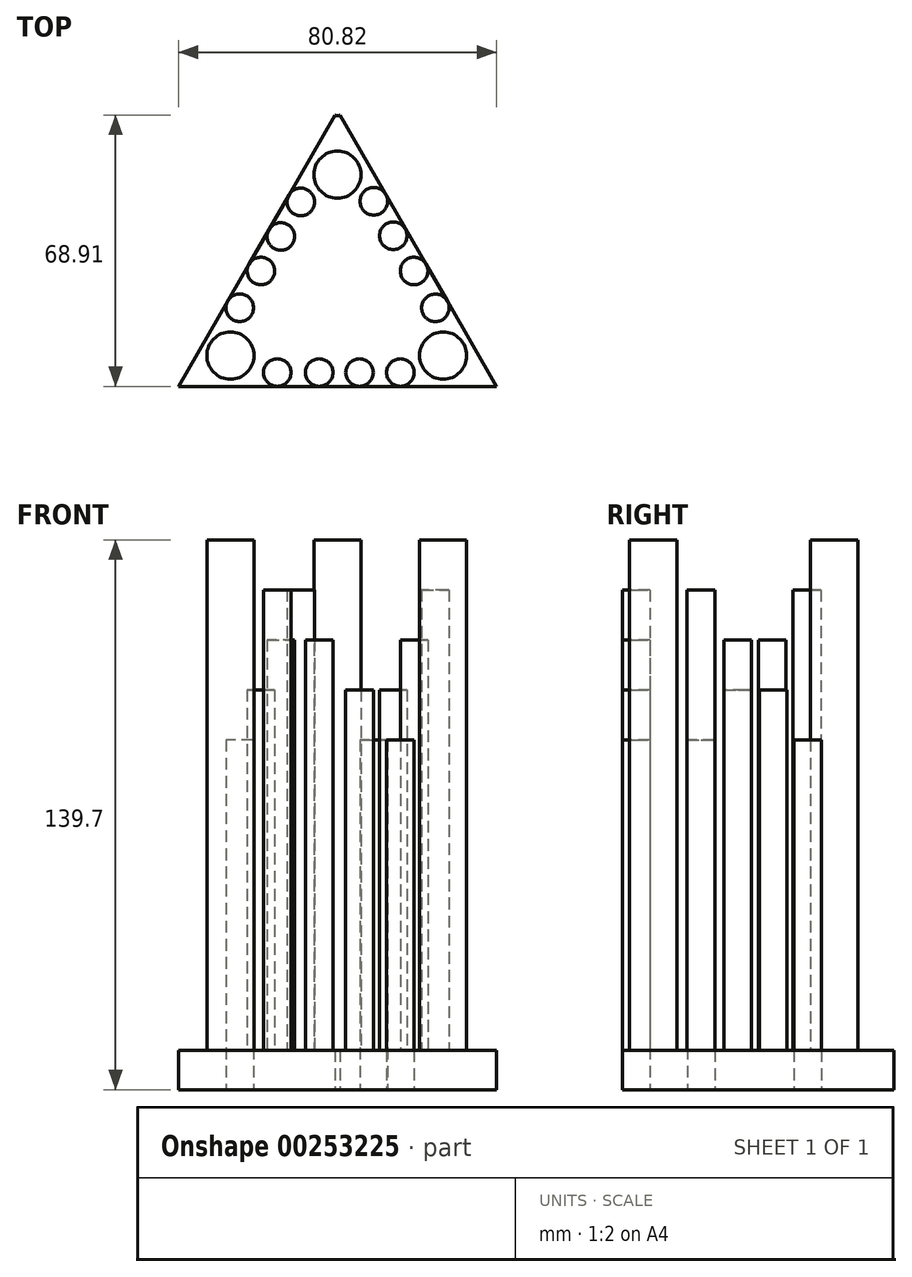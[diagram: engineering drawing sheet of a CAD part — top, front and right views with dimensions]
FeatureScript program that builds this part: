
annotation { "Feature Type Name" : "Feature", "Feature Type Description" : "" }
export const myFeature = defineFeature(function(context is Context, id is Id, definition is map)
    precondition{}
    {
        {
            var Q0;
            Q0=qCreatedBy(makeId("Top.planeOp"),FACE);
            var sketch = newSketch(context, id + "F0", { "sketchPlane" : qUnion([Q0])});
            skCircle(sketch, "E0.cCircle", {"center": v(0, 0) * mm, "radius": 23.33 * mm, "construction": true});
            skLineSegment(sketch, "E0.0", {"start": v(40.41, -23.33) * mm, "end": v(0, 46.67) * mm});
            skLineSegment(sketch, "E0.1", {"start": v(40.41, -23.33) * mm, "end": v(-40.41, -23.33) * mm});
            skLineSegment(sketch, "E0.2", {"start": v(0, 46.67) * mm, "end": v(-40.41, -23.33) * mm});
            skPoint(sketch, "E0.0.midPoint", {"position": v(20.2, 11.67) * mm});
            skCircle(sketch, "E1", {"center": v(0, 46.67) * mm, "radius": 1.25 * mm});
            skCircle(sketch, "E2", {"center": v(0, 30.46) * mm, "radius": 6 * mm});
            skCircle(sketch, "E3", {"center": v(-27.2, -15.52) * mm, "radius": 6 * mm});
            skCircle(sketch, "E4", {"center": v(26.82, -15.52) * mm, "radius": 6 * mm});
            skCircle(sketch, "E5", {"center": v(9.23, 23.69) * mm, "radius": 3.5 * mm});
            skCircle(sketch, "E6", {"center": v(14.17, 14.94) * mm, "radius": 3.5 * mm});
            skCircle(sketch, "E7", {"center": v(19.46, 5.97) * mm, "radius": 3.5 * mm});
            skCircle(sketch, "E8", {"center": v(15.98, -19.83) * mm, "radius": 3.5 * mm});
            skCircle(sketch, "E9", {"center": v(24.87, -3.4) * mm, "radius": 3.5 * mm});
            skCircle(sketch, "E10", {"center": v(-9.32, 23.52) * mm, "radius": 3.5 * mm});
            skCircle(sketch, "E11", {"center": v(-14.4, 14.74) * mm, "radius": 3.5 * mm});
            skCircle(sketch, "E12", {"center": v(-19.45, 5.97) * mm, "radius": 3.5 * mm});
            skCircle(sketch, "E13", {"center": v(-24.85, -3.37) * mm, "radius": 3.5 * mm});
            skCircle(sketch, "E14", {"center": v(5.6, -19.83) * mm, "radius": 3.5 * mm});
            skCircle(sketch, "E15", {"center": v(-4.66, -19.83) * mm, "radius": 3.5 * mm});
            skCircle(sketch, "E16", {"center": v(-15.31, -19.83) * mm, "radius": 3.5 * mm});
            skSolve(sketch);
        }
        {
            var Q0;
            Q0=makeQuery(id+"F0.imprint","IMPRINT",FACE,{"disambiguationData":[TD([[makeQuery(id+"F0.imprint","IMPRINT",EDGE,{"derivedFrom":sQuery(id+"F0.wireOp",EDGE,"E2")}),-1.0]])]});
            var Q1;
            Q1=makeQuery(id+"F0.imprint","IMPRINT",FACE,{"disambiguationData":[TD([[makeQuery(id+"F0.imprint","IMPRINT",EDGE,{"derivedFrom":sQuery(id+"F0.wireOp",EDGE,"E2")}),1.0]])]});
            var Q2;
            Q2=makeQuery(id+"F0.imprint","IMPRINT",FACE,{"disambiguationData":[TD([[makeQuery(id+"F0.imprint","IMPRINT",EDGE,{"derivedFrom":sQuery(id+"F0.wireOp",EDGE,"E5")}),1.0]])]});
            var Q3;
            Q3=makeQuery(id+"F0.imprint","IMPRINT",FACE,{"disambiguationData":[TD([[makeQuery(id+"F0.imprint","IMPRINT",EDGE,{"derivedFrom":sQuery(id+"F0.wireOp",EDGE,"E6")}),1.0]])]});
            var Q4;
            Q4=makeQuery(id+"F0.imprint","IMPRINT",FACE,{"disambiguationData":[TD([[makeQuery(id+"F0.imprint","IMPRINT",EDGE,{"derivedFrom":sQuery(id+"F0.wireOp",EDGE,"E7")}),1.0]])]});
            var Q5;
            Q5=makeQuery(id+"F0.imprint","IMPRINT",FACE,{"disambiguationData":[TD([[makeQuery(id+"F0.imprint","IMPRINT",EDGE,{"derivedFrom":sQuery(id+"F0.wireOp",EDGE,"E9")}),1.0]])]});
            var Q6;
            Q6=makeQuery(id+"F0.imprint","IMPRINT",FACE,{"disambiguationData":[TD([[makeQuery(id+"F0.imprint","IMPRINT",EDGE,{"derivedFrom":sQuery(id+"F0.wireOp",EDGE,"E4")}),1.0]])]});
            var Q7;
            Q7=makeQuery(id+"F0.imprint","IMPRINT",FACE,{"disambiguationData":[TD([[makeQuery(id+"F0.imprint","IMPRINT",EDGE,{"derivedFrom":sQuery(id+"F0.wireOp",EDGE,"E8")}),1.0]])]});
            var Q8;
            Q8=makeQuery(id+"F0.imprint","IMPRINT",FACE,{"disambiguationData":[TD([[makeQuery(id+"F0.imprint","IMPRINT",EDGE,{"derivedFrom":sQuery(id+"F0.wireOp",EDGE,"E14")}),1.0]])]});
            var Q9;
            Q9=makeQuery(id+"F0.imprint","IMPRINT",FACE,{"disambiguationData":[TD([[makeQuery(id+"F0.imprint","IMPRINT",EDGE,{"derivedFrom":sQuery(id+"F0.wireOp",EDGE,"E15")}),1.0]])]});
            var Q10;
            Q10=makeQuery(id+"F0.imprint","IMPRINT",FACE,{"disambiguationData":[TD([[makeQuery(id+"F0.imprint","IMPRINT",EDGE,{"derivedFrom":sQuery(id+"F0.wireOp",EDGE,"E16")}),1.0]])]});
            var Q11;
            Q11=makeQuery(id+"F0.imprint","IMPRINT",FACE,{"disambiguationData":[TD([[makeQuery(id+"F0.imprint","IMPRINT",EDGE,{"derivedFrom":sQuery(id+"F0.wireOp",EDGE,"E3")}),1.0]])]});
            var Q12;
            Q12=makeQuery(id+"F0.imprint","IMPRINT",FACE,{"disambiguationData":[TD([[makeQuery(id+"F0.imprint","IMPRINT",EDGE,{"derivedFrom":sQuery(id+"F0.wireOp",EDGE,"E13")}),1.0]])]});
            var Q13;
            Q13=makeQuery(id+"F0.imprint","IMPRINT",FACE,{"disambiguationData":[TD([[makeQuery(id+"F0.imprint","IMPRINT",EDGE,{"derivedFrom":sQuery(id+"F0.wireOp",EDGE,"E12")}),1.0]])]});
            var Q14;
            Q14=makeQuery(id+"F0.imprint","IMPRINT",FACE,{"disambiguationData":[TD([[makeQuery(id+"F0.imprint","IMPRINT",EDGE,{"derivedFrom":sQuery(id+"F0.wireOp",EDGE,"E11")}),1.0]])]});
            var Q15;
            Q15=makeQuery(id+"F0.imprint","IMPRINT",FACE,{"disambiguationData":[TD([[makeQuery(id+"F0.imprint","IMPRINT",EDGE,{"derivedFrom":sQuery(id+"F0.wireOp",EDGE,"E10")}),1.0]])]});
            extrude(context, id + "F1", {"entities" : qUnion([Q0, Q1, Q2, Q3, Q4, Q5, Q6, Q7, Q8, Q9, Q10, Q11, Q12, Q13, Q14, Q15]), "depth" : 10 * mm});
        }
        {
            var Q0;
            Q0=makeQuery(id+"F0.imprint","IMPRINT",FACE,{"disambiguationData":[TD([[makeQuery(id+"F0.imprint","IMPRINT",EDGE,{"derivedFrom":sQuery(id+"F0.wireOp",EDGE,"E5")}),1.0]])]});
            var Q1;
            Q1=makeQuery(id+"F0.imprint","IMPRINT",FACE,{"disambiguationData":[TD([[makeQuery(id+"F0.imprint","IMPRINT",EDGE,{"derivedFrom":sQuery(id+"F0.wireOp",EDGE,"E8")}),1.0]])]});
            var Q2;
            Q2=makeQuery(id+"F0.imprint","IMPRINT",FACE,{"disambiguationData":[TD([[makeQuery(id+"F0.imprint","IMPRINT",EDGE,{"derivedFrom":sQuery(id+"F0.wireOp",EDGE,"E13")}),1.0]])]});
            extrude(context, id + "F2", {"entities" : qUnion([Q0, Q1, Q2]), "depth" : 88.9 * mm});
        }
        {
            var Q0;
            Q0=makeQuery(id+"F0.imprint","IMPRINT",FACE,{"disambiguationData":[TD([[makeQuery(id+"F0.imprint","IMPRINT",EDGE,{"derivedFrom":sQuery(id+"F0.wireOp",EDGE,"E12")}),1.0]])]});
            var Q1;
            Q1=makeQuery(id+"F0.imprint","IMPRINT",FACE,{"disambiguationData":[TD([[makeQuery(id+"F0.imprint","IMPRINT",EDGE,{"derivedFrom":sQuery(id+"F0.wireOp",EDGE,"E6")}),1.0]])]});
            var Q2;
            Q2=makeQuery(id+"F0.imprint","IMPRINT",FACE,{"disambiguationData":[TD([[makeQuery(id+"F0.imprint","IMPRINT",EDGE,{"derivedFrom":sQuery(id+"F0.wireOp",EDGE,"E14")}),1.0]])]});
            extrude(context, id + "F3", {"entities" : qUnion([Q0, Q1, Q2]), "operationType" : NewBodyOperationType.ADD, "depth" : 101.6 * mm});
        }
        {
            var Q0;
            Q0=makeQuery(id+"F0.imprint","IMPRINT",FACE,{"disambiguationData":[TD([[makeQuery(id+"F0.imprint","IMPRINT",EDGE,{"derivedFrom":sQuery(id+"F0.wireOp",EDGE,"E15")}),1.0]])]});
            var Q1;
            Q1=makeQuery(id+"F0.imprint","IMPRINT",FACE,{"disambiguationData":[TD([[makeQuery(id+"F0.imprint","IMPRINT",EDGE,{"derivedFrom":sQuery(id+"F0.wireOp",EDGE,"E11")}),1.0]])]});
            var Q2;
            Q2=makeQuery(id+"F0.imprint","IMPRINT",FACE,{"disambiguationData":[TD([[makeQuery(id+"F0.imprint","IMPRINT",EDGE,{"derivedFrom":sQuery(id+"F0.wireOp",EDGE,"E7")}),1.0]])]});
            extrude(context, id + "F4", {"entities" : qUnion([Q0, Q1, Q2]), "operationType" : NewBodyOperationType.ADD, "depth" : 114.3 * mm});
        }
        {
            var Q0;
            Q0=makeQuery(id+"F0.imprint","IMPRINT",FACE,{"disambiguationData":[TD([[makeQuery(id+"F0.imprint","IMPRINT",EDGE,{"derivedFrom":sQuery(id+"F0.wireOp",EDGE,"E16")}),1.0]])]});
            var Q1;
            Q1=makeQuery(id+"F0.imprint","IMPRINT",FACE,{"disambiguationData":[TD([[makeQuery(id+"F0.imprint","IMPRINT",EDGE,{"derivedFrom":sQuery(id+"F0.wireOp",EDGE,"E10")}),1.0]])]});
            var Q2;
            Q2=makeQuery(id+"F0.imprint","IMPRINT",FACE,{"disambiguationData":[TD([[makeQuery(id+"F0.imprint","IMPRINT",EDGE,{"derivedFrom":sQuery(id+"F0.wireOp",EDGE,"E9")}),1.0]])]});
            extrude(context, id + "F5", {"entities" : qUnion([Q0, Q1, Q2]), "operationType" : NewBodyOperationType.ADD, "depth" : 127 * mm});
        }
        {
            var Q0;
            Q0=makeQuery(id+"F0.imprint","IMPRINT",FACE,{"disambiguationData":[TD([[makeQuery(id+"F0.imprint","IMPRINT",EDGE,{"derivedFrom":sQuery(id+"F0.wireOp",EDGE,"E3")}),1.0]])]});
            var Q1;
            Q1=makeQuery(id+"F0.imprint","IMPRINT",FACE,{"disambiguationData":[TD([[makeQuery(id+"F0.imprint","IMPRINT",EDGE,{"derivedFrom":sQuery(id+"F0.wireOp",EDGE,"E2")}),1.0]])]});
            var Q2;
            Q2=makeQuery(id+"F0.imprint","IMPRINT",FACE,{"disambiguationData":[TD([[makeQuery(id+"F0.imprint","IMPRINT",EDGE,{"derivedFrom":sQuery(id+"F0.wireOp",EDGE,"E4")}),1.0]])]});
            extrude(context, id + "F6", {"entities" : qUnion([Q0, Q1, Q2]), "operationType" : NewBodyOperationType.ADD, "depth" : 139.7 * mm});
        }
    });
